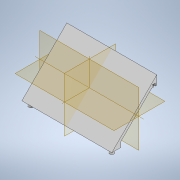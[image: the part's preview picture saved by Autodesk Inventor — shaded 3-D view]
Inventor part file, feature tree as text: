
AUTODESK INVENTOR PART (.ipt)
format: ipt  version: 2022.4 (Build 264492010, 492A)  size: 156,160 bytes
history: native  units: mm
features: revolve x4, sketch x3, extrude x2
ambient origin geometry x8: Origin, YZ Plane, XZ Plane, XY Plane, X Axis, Y Axis, Z Axis, Center Point
bodies: Solid1 (feature_tree)
feature tree (9):
  extrude  "Extrusion1"  Depth=50.0mm
  sketch  "Sketch4"  dims[d2=3.0mm d3=100.0mm d4=0.0mm]
  revolve  "Revolution2"  [1 undecoded]
  revolve  "Revolution3"  [1 undecoded]
  revolve  "Revolution4"  [1 undecoded]
  revolve  "Revolution5"  [1 undecoded]
  extrude  "Extrusion3"  Depth=3.0mm
  sketch  "Sketch1"  dims[d0=50.0mm d1=50.0mm]
  sketch  "Sketch5"  dims[d5=10.0mm d45=3.0mm d46=5.0mm d47=5.0mm d48=3.0mm d56=360.0deg d57=360.0deg d58=360.0deg d59=360.0deg d73=5.0mm d74=5.0mm d90=5.0mm d91=0.0mm d92=3.0mm d93=1.6mm d94=1.6mm d95=1.6mm d96=1.6mm d97=1.6mm d98=3.0mm d99=5.0mm d100=30.0mm d101=3.0mm d102=20.0mm d104=60.0mm d105=10.0mm d107=10.0mm]
note: 4 required parameter values undecoded (feature->parameter linkage not recoverable at this tier; creation-order binding heuristic only, values carry confidence <= 0.55)
